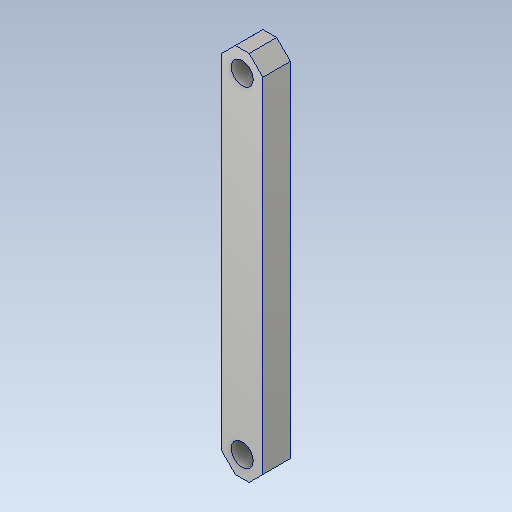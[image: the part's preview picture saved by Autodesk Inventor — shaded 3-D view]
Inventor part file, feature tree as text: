
AUTODESK INVENTOR PART (.ipt)
format: ipt  version: 2020 (Build 240168000, 168)  size: 107,520 bytes
history: native  units: mm
features: extrude x2, sketch x2, other x1, chamfer x1, projected_geometry x1
ambient origin geometry x8: Origin, YZ Plane, XZ Plane, XY Plane, X Axis, Y Axis, Z Axis, Center Point
bodies: Body1 (feature_tree)
feature tree (7):
  other  "솔리드1"
  extrude  "돌출1"  Depth=6.0mm
  extrude  "돌출2"  Depth=54.0mm
  chamfer  "모따기1"  Distance=3.0mm
  sketch  "스케치1"
  sketch  "스케치2"
  projected_geometry  "투영된 루프1"
